# Revit family: Lighting_Outside_L-L-Luce-Light_Plin-2
name_source: partatom
category: Lighting Fixtures
units: mm (PartAtom-declared; Revit-internal decimal feet)

## family parameters
Always vertical = No
Cut with Voids When Loaded = No
Light Source = Yes
OmniClass Number = 23.80.70.00
OmniClass Title = Lighting
Part Type = Normal
Room Calculation Point = No
Round Connector Dimension = Use Diameter
Shared = No
Work Plane-Based = Yes

## types (3) — shared parameters
Body = Head and column in aluminium
Color Filter = 16777215
Default Elevation = 1219 mm
Dimming Lamp Color Temperature Shift = <None>
Emit Shape Visible in Rendering = No
Emit from Rectangle Length = 110 mm  [stored 0.360892 ft]
Emit from Rectangle Width = 24 mm  [stored 0.0787402 ft]
Installation instructions = https://www.lucelight.it
Luce-Light_Applications = floor
Luce-Light_Body_material = aluminium
Luce-Light_Classification = CE
Luce-Light_Color_Rendering_Index_CRI = 80
Luce-Light_Finishes_material = grey, white, anthracite, cor-ten
Luce-Light_IK = 08
Luce-Light_IP = 65
Luce-Light_LED_colour = 2700K, 3000K, 4000K
Luce-Light_LED_light_sources = 18 mid power LEDs, 3-step MacAdam, 50 000h L85 B10 (Ta 25°C)
Luce-Light_Mounting = surface mounted
Luce-Light_Note = non-standard heights available on request
Luce-Light_Optical_assembly = diffuse, asymmetrical
Luce-Light_Power = 12W
Luce-Light_Power_Class = 230Vac
Luce-Light_Screen_material = serigraphed, tempered extra-clear glass
Luce-Light_Total_flow_rate = 492 lm (3000K)
Luce-Light_lumen-output-at-source = 1242 lm (3000K)
Manufacturer = L&L Luce&Light
Material = Metal-Luce&Light-Aluminium
Nominal height = 560 mm
Nominal width = 124 mm
Product Guid = d8eb926a-e6bf-489d-a820-188e9db58a78
Product data url = https://www.bimobject.com
Product url = https://www.lucelight.it
Secondary material = Screen in glass
Technical description = https://www.lucelight.it
Tilt Angle = 90.00°
URL = https://www.lucelight.it
Wattage Comments = 12W

## per-type parameters (varying)
| type | Photometric Web File |
| PLIN 2.1 A 3000K 12W 230Vac h560 | PLIN 2.1 A [3000K 12W 230Vac] h560.IES |
| PLIN 2.1 A 2700K 12W 230Vac h560 | PLIN 2.1 A [2700K 12W 230Vac] h560.IES |
| PLIN 2.1 A 4000K 12W 230Vac h560 | PLIN 2.1 A [4000K 12W 230Vac] h560.IES |

note: [stored X ft] marks values corroborated as IEEE doubles in the binary element streams (Revit-internal decimal feet)

## geometry (parser evidence)
native form markers: Blend x4, Sweep x4
no freeform markers — native parametric forms only
